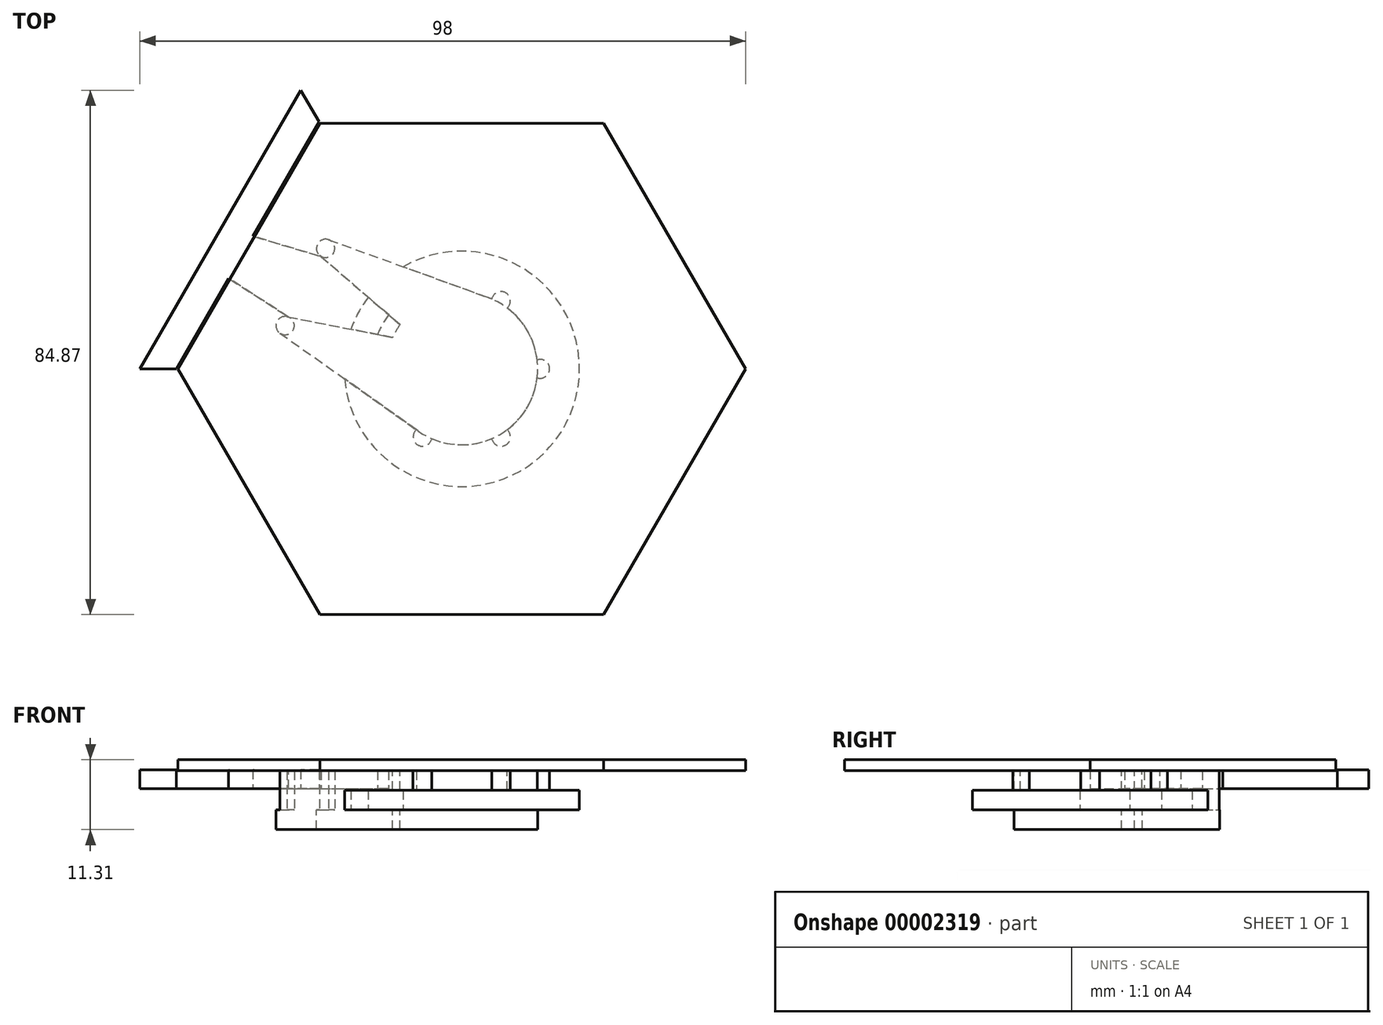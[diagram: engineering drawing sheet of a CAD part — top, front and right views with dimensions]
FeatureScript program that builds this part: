
annotation { "Feature Type Name" : "Feature", "Feature Type Description" : "" }
export const myFeature = defineFeature(function(context is Context, id is Id, definition is map)
    precondition{}
    {
        {
            var Q0;
            Q0=qCreatedBy(makeId("Top.planeOp"),FACE);
            var sketch = newSketch(context, id + "F0", { "sketchPlane" : qUnion([Q0])});
            skCircle(sketch, "E0.cCircle", {"center": v(0, 0) * mm, "radius": 39.77 * mm, "construction": true});
            skLineSegment(sketch, "E0.0", {"start": v(-45.92, 0) * mm, "end": v(-22.96, 39.77) * mm});
            skLineSegment(sketch, "E0.1", {"start": v(-22.96, 39.77) * mm, "end": v(22.96, 39.77) * mm});
            skLineSegment(sketch, "E0.2", {"start": v(22.96, 39.77) * mm, "end": v(45.92, 0) * mm});
            skLineSegment(sketch, "E0.3", {"start": v(45.92, 0) * mm, "end": v(22.96, -39.77) * mm});
            skLineSegment(sketch, "E0.4", {"start": v(22.96, -39.77) * mm, "end": v(-22.96, -39.77) * mm});
            skLineSegment(sketch, "E0.5", {"start": v(-22.96, -39.77) * mm, "end": v(-45.92, 0) * mm});
            skPoint(sketch, "E0.0.midPoint", {"position": v(-34.44, 19.89) * mm});
            skSolve(sketch);
        }
        {
            var Q0;
            Q0=makeQuery(id+"F0.imprint","IMPRINT",FACE,{"disambiguationData":[TD([[makeQuery(id+"F0.imprint","IMPRINT",EDGE,{"derivedFrom":sQuery(id+"F0.wireOp",EDGE,"E0.0")}),-1.0]])]});
            extrude(context, id + "F1", {"entities" : qUnion([Q0]), "depth" : 1.78 * mm});
        }
        {
            var Q0;
            Q0=makeQuery(id+"F1.opExtrude","CAP_FACE",FACE,{"disambiguationData":[OSD([sQuery(id+"F0.wireOp",EDGE,"E0.0"),sQuery(id+"F0.wireOp",EDGE,"E0.1"),sQuery(id+"F0.wireOp",EDGE,"E0.2"),sQuery(id+"F0.wireOp",EDGE,"E0.3"),sQuery(id+"F0.wireOp",EDGE,"E0.4"),sQuery(id+"F0.wireOp",EDGE,"E0.5")])],"isStart":false});
            var sketch = newSketch(context, id + "F2", { "sketchPlane" : qUnion([Q0])});
            skLineSegment(sketch, "E1.0", {"start": v(-45.92, 0) * mm, "end": v(-22.96, 39.77) * mm, "construction": true});
            skLineSegment(sketch, "E1.1", {"start": v(-22.96, 39.77) * mm, "end": v(22.96, 39.77) * mm, "construction": true});
            skLineSegment(sketch, "E1.2", {"start": v(22.96, 39.77) * mm, "end": v(45.92, 0) * mm, "construction": true});
            skLineSegment(sketch, "E1.3", {"start": v(45.92, 0) * mm, "end": v(22.96, -39.77) * mm, "construction": true});
            skLineSegment(sketch, "E1.4", {"start": v(22.96, -39.77) * mm, "end": v(-22.96, -39.77) * mm, "construction": true});
            skLineSegment(sketch, "E1.5", {"start": v(-22.96, -39.77) * mm, "end": v(-45.92, 0) * mm, "construction": true});
            skLineSegment(sketch, "E2.0", {"start": v(-23.1, 40.02) * mm, "end": v(23.1, 40.02) * mm});
            skLineSegment(sketch, "E2.1", {"start": v(-46.22, 0) * mm, "end": v(-23.1, 40.02) * mm});
            skLineSegment(sketch, "E2.2", {"start": v(-23.1, -40.02) * mm, "end": v(-46.22, 0) * mm});
            skLineSegment(sketch, "E2.3", {"start": v(23.1, -40.02) * mm, "end": v(-23.1, -40.02) * mm});
            skLineSegment(sketch, "E2.4", {"start": v(46.22, 0) * mm, "end": v(23.1, -40.02) * mm});
            skLineSegment(sketch, "E2.5", {"start": v(23.1, 40.02) * mm, "end": v(46.22, 0) * mm});
            skLineSegment(sketch, "E3.0", {"start": v(-52.08, 0) * mm, "end": v(-26.04, 45.1) * mm});
            skLineSegment(sketch, "E3.1", {"start": v(-26.04, -45.1) * mm, "end": v(-52.08, 0) * mm});
            skLineSegment(sketch, "E3.2", {"start": v(26.04, -45.1) * mm, "end": v(-26.04, -45.1) * mm});
            skLineSegment(sketch, "E3.3", {"start": v(52.08, 0) * mm, "end": v(26.04, -45.1) * mm});
            skLineSegment(sketch, "E3.4", {"start": v(26.04, 45.1) * mm, "end": v(52.08, 0) * mm});
            skLineSegment(sketch, "E3.5", {"start": v(-26.04, 45.1) * mm, "end": v(26.04, 45.1) * mm});
            skSolve(sketch);
        }
        {
            var Q0;
            Q0=makeQuery(id+"F1.opExtrude","CAP_FACE",FACE,{"disambiguationData":[OSD([sQuery(id+"F0.wireOp",EDGE,"E0.0"),sQuery(id+"F0.wireOp",EDGE,"E0.1"),sQuery(id+"F0.wireOp",EDGE,"E0.2"),sQuery(id+"F0.wireOp",EDGE,"E0.3"),sQuery(id+"F0.wireOp",EDGE,"E0.4"),sQuery(id+"F0.wireOp",EDGE,"E0.5")])],"isStart":true});
            cPlane(context, id + "F3", {"entities" : qUnion([Q0]), "cplaneType" : CPlaneType.OFFSET, "offset" : 6.35 * mm, "width" : 152.4 * mm, "height" : 152.4 * mm});
        }
        {
            var Q0;
            Q0=qCreatedBy(id+"F3.planeOp",FACE);
            var sketch = newSketch(context, id + "F4", { "sketchPlane" : qUnion([Q0])});
            skCircle(sketch, "E4", {"center": v(0, 0) * mm, "radius": 19.05 * mm});
            skCircle(sketch, "E5", {"center": v(0, 0) * mm, "radius": 1.59 * mm});
            skCircle(sketch, "E6.0", {"center": v(0, 0) * mm, "radius": 12.7 * mm, "construction": true});
            skCircle(sketch, "E7.0", {"center": v(0, 0) * mm, "radius": 19.05 * mm, "construction": true});
            skLineSegment(sketch, "E8.0", {"start": v(6.35, -11) * mm, "end": v(-6.35, -11) * mm, "construction": true});
            skLineSegment(sketch, "E8.1", {"start": v(-6.35, -11) * mm, "end": v(-12.7, 0) * mm, "construction": true});
            skLineSegment(sketch, "E8.2", {"start": v(-12.7, 0) * mm, "end": v(-6.35, 11) * mm, "construction": true});
            skLineSegment(sketch, "E8.3", {"start": v(-6.35, 11) * mm, "end": v(6.35, 11) * mm, "construction": true});
            skLineSegment(sketch, "E8.4", {"start": v(6.35, 11) * mm, "end": v(12.7, 0) * mm, "construction": true});
            skLineSegment(sketch, "E8.5", {"start": v(12.7, 0) * mm, "end": v(6.35, -11) * mm, "construction": true});
            skCircle(sketch, "E9", {"center": v(-6.35, -11) * mm, "radius": 1.52 * mm});
            skSolve(sketch);
        }
        {
            var Q0;
            Q0=makeQuery(id+"F4.imprint","IMPRINT",FACE,{"disambiguationData":[TD([[makeQuery(id+"F4.imprint","IMPRINT",EDGE,{"derivedFrom":sQuery(id+"F4.wireOp",EDGE,"E4")}),1.0]])]});
            var Q1;
            Q1=makeQuery(id+"F4.imprint","IMPRINT",FACE,{"disambiguationData":[TD([[makeQuery(id+"F4.imprint","IMPRINT",EDGE,{"derivedFrom":sQuery(id+"F4.wireOp",EDGE,"E9")}),1.0]])]});
            extrude(context, id + "F5", {"entities" : qUnion([Q0, Q1]), "oppositeDirection" : true, "depth" : 3.17 * mm});
        }
        {
            var Q0;
            Q0=makeQuery(id+"F4.imprint","IMPRINT",FACE,{"disambiguationData":[TD([[makeQuery(id+"F4.imprint","IMPRINT",EDGE,{"derivedFrom":sQuery(id+"F4.wireOp",EDGE,"E9")}),1.0]])]});
            extrude(context, id + "F6", {"entities" : qUnion([Q0]), "operationType" : NewBodyOperationType.ADD, "oppositeDirection" : true, "depth" : 6.35 * mm});
        }
        {
            var Q0;
            Q0=makeQuery(id+"F5.opExtrude","CAP_FACE",FACE,{"disambiguationData":[OSD([sQuery(id+"F4.wireOp",EDGE,"E4"),sQuery(id+"F4.wireOp",EDGE,"E5")])],"isStart":false});
            cPlane(context, id + "F7", {"entities" : qUnion([Q0]), "cplaneType" : CPlaneType.OFFSET, "offset" : 0.25 * mm, "width" : 152.4 * mm, "height" : 152.4 * mm});
        }
        {
            var Q0;
            Q0=makeQuery(id+"F6.opExtrude","CAP_FACE",FACE,{"disambiguationData":[OSD([sQuery(id+"F4.wireOp",EDGE,"E9")])],"isStart":false});
            var Q1;
            Q1=makeQuery(id+"F6.opExtrude","SWEPT_FACE",FACE,{"disambiguationData":[OSD([sQuery(id+"F4.wireOp",EDGE,"E9")])]});
            var Q2;
            Q2=makeQuery(id+"F5.opExtrude","CAP_EDGE",EDGE,{"disambiguationData":[OSD([sQuery(id+"F4.wireOp",EDGE,"E5")])],"isStart":false});
            circularPattern(context, id + "F8", {"faces" : qUnion([Q0, Q1]), "axis" : qUnion([Q2]), "angle" : 360 * degree, "instanceCount" : 6, "equalSpace" : true, "patternType" : PatternType.FACE});
        }
        {
            var Q0;
            Q0=qCreatedBy(id+"F7.planeOp",FACE);
            var sketch = newSketch(context, id + "F9", { "sketchPlane" : qUnion([Q0])});
            skCircle(sketch, "E10.0", {"center": v(-6.35, 11) * mm, "radius": 1.52 * mm, "construction": true});
            skCircle(sketch, "E11.0", {"center": v(-6.35, 11) * mm, "radius": 2.03 * mm, "construction": true});
            skLineSegment(sketch, "E12.0", {"start": v(-52.08, 0) * mm, "end": v(-26.04, 45.1) * mm});
            skLineSegment(sketch, "E12.1", {"start": v(-46.22, 0) * mm, "end": v(-37.75, 14.66) * mm});
            skLineSegment(sketch, "E13", {"start": v(-46.22, 0) * mm, "end": v(-52.08, 0) * mm});
            skLineSegment(sketch, "E14", {"start": v(-23.1, 40.02) * mm, "end": v(-26.04, 45.1) * mm});
            skLineSegment(sketch, "E15.trimOffspring", {"start": v(-33.82, 21.48) * mm, "end": v(-23.1, 40.02) * mm});
            skCircle(sketch, "E16.0", {"center": v(0, 0) * mm, "radius": 1.59 * mm, "construction": true});
            skArc(sketch, "E17", {"start": v(-10.23, 10.6) * mm, "mid": v(-12.76, 7.37) * mm, "end": v(-14.3, 3.56) * mm});
            skArc(sketch, "E18", {"start": v(-7.41, 7.67) * mm, "mid": v(-9.24, 5.33) * mm, "end": v(-10.35, 2.58) * mm});
            skLineSegment(sketch, "E19", {"start": v(0, 0) * mm, "end": v(-25.92, 0) * mm, "construction": true});
            skLineSegment(sketch, "E20", {"start": v(0, 0) * mm, "end": v(23.79, 0) * mm, "construction": true});
            skLineSegment(sketch, "E21.0", {"start": v(-12.7, 0) * mm, "end": v(-6.35, -11) * mm, "construction": true});
            skLineSegment(sketch, "E21.1", {"start": v(-6.35, -11) * mm, "end": v(6.35, -11) * mm, "construction": true});
            skLineSegment(sketch, "E21.2", {"start": v(6.35, -11) * mm, "end": v(12.7, 0) * mm, "construction": true});
            skLineSegment(sketch, "E21.3", {"start": v(12.7, 0) * mm, "end": v(6.35, 11) * mm, "construction": true});
            skLineSegment(sketch, "E21.4", {"start": v(6.35, 11) * mm, "end": v(-6.35, 11) * mm, "construction": true});
            skLineSegment(sketch, "E21.5", {"start": v(-6.35, 11) * mm, "end": v(-12.7, 0) * mm, "construction": true});
            skLineSegment(sketch, "E22", {"start": v(0, 0) * mm, "end": v(-6.35, 11) * mm, "construction": true});
            skLineSegment(sketch, "E23", {"start": v(0, 0) * mm, "end": v(6.35, 11) * mm, "construction": true});
            skLineSegment(sketch, "E24", {"start": v(0, 0) * mm, "end": v(6.35, -11) * mm, "construction": true});
            skLineSegment(sketch, "E25", {"start": v(0, 0) * mm, "end": v(-6.35, -11) * mm, "construction": true});
            skArc(sketch, "E26", {"start": v(-6.35, 11) * mm, "mid": v(-11, 6.35) * mm, "end": v(-12.7, 0) * mm, "construction": true});
            skLineSegment(sketch, "E27", {"start": v(0, 0) * mm, "end": v(-21.35, 5.32) * mm, "construction": true});
            skLineSegment(sketch, "E28", {"start": v(0, 0) * mm, "end": v(-16.03, 16.6) * mm, "construction": true});
            skArc(sketch, "E29", {"start": v(-14.3, 3.56) * mm, "mid": v(-12.81, 1.1) * mm, "end": v(-10.35, 2.58) * mm});
            skArc(sketch, "E30", {"start": v(-7.41, 7.67) * mm, "mid": v(-7.36, 10.55) * mm, "end": v(-10.23, 10.6) * mm});
            skArc(sketch, "E31.1", {"start": v(-4.83, 5.17) * mm, "mid": v(-4.01, 12.05) * mm, "end": v(-10.5, 14.5) * mm});
            skArc(sketch, "E31.2", {"start": v(-4.83, 5.17) * mm, "mid": v(-6.27, 3.33) * mm, "end": v(-7.07, 1.13) * mm});
            skArc(sketch, "E31.3", {"start": v(-17.81, 1.83) * mm, "mid": v(-12.7, -2.53) * mm, "end": v(-7.07, 1.13) * mm});
            skLineSegment(sketch, "E32", {"start": v(-17.81, 1.83) * mm, "end": v(-37.75, 14.66) * mm});
            skLineSegment(sketch, "E33", {"start": v(-10.5, 14.5) * mm, "end": v(-33.82, 21.48) * mm});
            skSolve(sketch);
        }
        {
            var Q0;
            Q0=makeQuery(id+"F9.imprint","IMPRINT",FACE,{"disambiguationData":[TD([[makeQuery(id+"F9.imprint","IMPRINT",EDGE,{"derivedFrom":sQuery(id+"F9.wireOp",EDGE,"E12.0")}),-1.0]])]});
            extrude(context, id + "F10", {"entities" : qUnion([Q0]), "depth" : 3.05 * mm});
        }
        {
            var Q0;
            Q0=makeQuery(id+"F4.imprint","IMPRINT",FACE,{"disambiguationData":[TD([[makeQuery(id+"F4.imprint","IMPRINT",EDGE,{"derivedFrom":sQuery(id+"F4.wireOp",EDGE,"E4")}),1.0]])]});
            var sketch = newSketch(context, id + "F11", { "sketchPlane" : qUnion([Q0])});
            skCircle(sketch, "E34.0", {"center": v(0, 0) * mm, "radius": 1.59 * mm, "construction": true});
            skCircle(sketch, "E35", {"center": v(0, 0) * mm, "radius": 30.9 * mm, "construction": true});
            skLineSegment(sketch, "E36.0", {"start": v(-17.81, -1.83) * mm, "end": v(-37.75, -14.66) * mm, "construction": true});
            skLineSegment(sketch, "E36.1", {"start": v(-10.5, -14.5) * mm, "end": v(-33.82, -21.48) * mm, "construction": true});
            skArc(sketch, "E37", {"start": v(-29.44, -5.8) * mm, "mid": v(-29.94, -7.58) * mm, "end": v(-28.3, -8.45) * mm});
            skArc(sketch, "E38", {"start": v(-23, -18.38) * mm, "mid": v(-23.31, -20.25) * mm, "end": v(-21.53, -20.9) * mm});
            skArc(sketch, "E39", {"start": v(-11.19, -5.1) * mm, "mid": v(-10.64, -6.16) * mm, "end": v(-9.99, -7.17) * mm});
            skLineSegment(sketch, "E40", {"start": v(-29.44, -5.8) * mm, "end": v(-7.1, 10.03) * mm});
            skLineSegment(sketch, "E41", {"start": v(-28.3, -8.45) * mm, "end": v(-11.19, -5.1) * mm});
            skLineSegment(sketch, "E42", {"start": v(-21.53, -20.9) * mm, "end": v(4.2, -11.56) * mm});
            skLineSegment(sketch, "E43", {"start": v(-23, -18.38) * mm, "end": v(-9.99, -7.17) * mm});
            skArc(sketch, "E44.trimOffspring", {"start": v(4.2, -11.56) * mm, "mid": v(10.9, 5.7) * mm, "end": v(-7.1, 10.03) * mm});
            skSolve(sketch);
        }
        {
            var Q0;
            {var subQ0=makeQuery(id+"F11.imprint","IMPRINT",EDGE,{"derivedFrom":makeQuery(id+"F4.imprint","IMPRINT",EDGE,{"derivedFrom":sQuery(id+"F4.wireOp",EDGE,"E5")})});var subQ1=makeQuery(id+"F11.imprint","IMPRINT",EDGE,{"derivedFrom":makeQuery(id+"F4.imprint","IMPRINT",EDGE,{"derivedFrom":sQuery(id+"F4.wireOp",EDGE,"E9")})});var subQ8=sQuery(id+"F11.wireOp",EDGE,"E37");var subQ14=sQuery(id+"F11.wireOp",EDGE,"E38");var subQ15=sQuery(id+"F11.wireOp",EDGE,"E39");Q0=qUnion([makeQuery(id+"F11.imprint","IMPRINT",FACE,{"disambiguationData":[TD([[subQ0,1.0]])]}),makeQuery(id+"F11.imprint","IMPRINT",FACE,{"disambiguationData":[TD([[subQ1,1.0]])]}),makeQuery(id+"F11.imprint","IMPRINT",FACE,{"disambiguationData":[TD([[makeQuery(id+"F11.imprint","IMPRINT",EDGE,{"derivedFrom":subQ8}),1.0]])]}),makeQuery(id+"F11.imprint","IMPRINT",FACE,{"disambiguationData":[TD([[makeQuery(id+"F11.imprint","IMPRINT",EDGE,{"derivedFrom":subQ14}),1.0]])]}),makeQuery(id+"F11.imprint","IMPRINT",FACE,{"disambiguationData":[TD([[makeQuery(id+"F11.imprint","IMPRINT",EDGE,{"derivedFrom":subQ15}),1.0]])]})]);}
            extrude(context, id + "F12", {"entities" : qUnion([Q0]), "depth" : 3.17 * mm});
        }
        {
            var Q0;
            Q0=makeQuery(id+"F12.opExtrude","CAP_FACE",FACE,{"disambiguationData":[OSD([sQuery(id+"F11.wireOp",EDGE,"E37"),sQuery(id+"F11.wireOp",EDGE,"E38"),sQuery(id+"F11.wireOp",EDGE,"E39"),sQuery(id+"F11.wireOp",EDGE,"E40"),sQuery(id+"F11.wireOp",EDGE,"E41"),sQuery(id+"F11.wireOp",EDGE,"E42"),sQuery(id+"F11.wireOp",EDGE,"E43"),sQuery(id+"F11.wireOp",EDGE,"E44.trimOffspring")])],"isStart":true});
            var sketch = newSketch(context, id + "F13", { "sketchPlane" : qUnion([Q0])});
            skCircle(sketch, "E45", {"center": v(-22.03, 19.5) * mm, "radius": 1.48 * mm});
            skCircle(sketch, "E46", {"center": v(-28.58, 7) * mm, "radius": 1.48 * mm});
            skSolve(sketch);
        }
        {
            var Q0;
            {var subQ0=sQuery(id+"F13.wireOp",EDGE,"E45");var subQ1=sQuery(id+"F13.wireOp",EDGE,"E46");Q0=qUnion([makeQuery(id+"F13.imprint","IMPRINT",FACE,{"disambiguationData":[TD([[makeQuery(id+"F13.imprint","IMPRINT",EDGE,{"disambiguationData":[OD(0.0)],"derivedFrom":subQ0}),-1.0]])]}),makeQuery(id+"F13.imprint","IMPRINT",FACE,{"disambiguationData":[TD([[makeQuery(id+"F13.imprint","IMPRINT",EDGE,{"disambiguationData":[OD(0.0)],"derivedFrom":subQ1}),-1.0]])]})]);}
            extrude(context, id + "F14", {"entities" : qUnion([Q0]), "operationType" : NewBodyOperationType.ADD, "depth" : 6.35 * mm});
        }
    });
